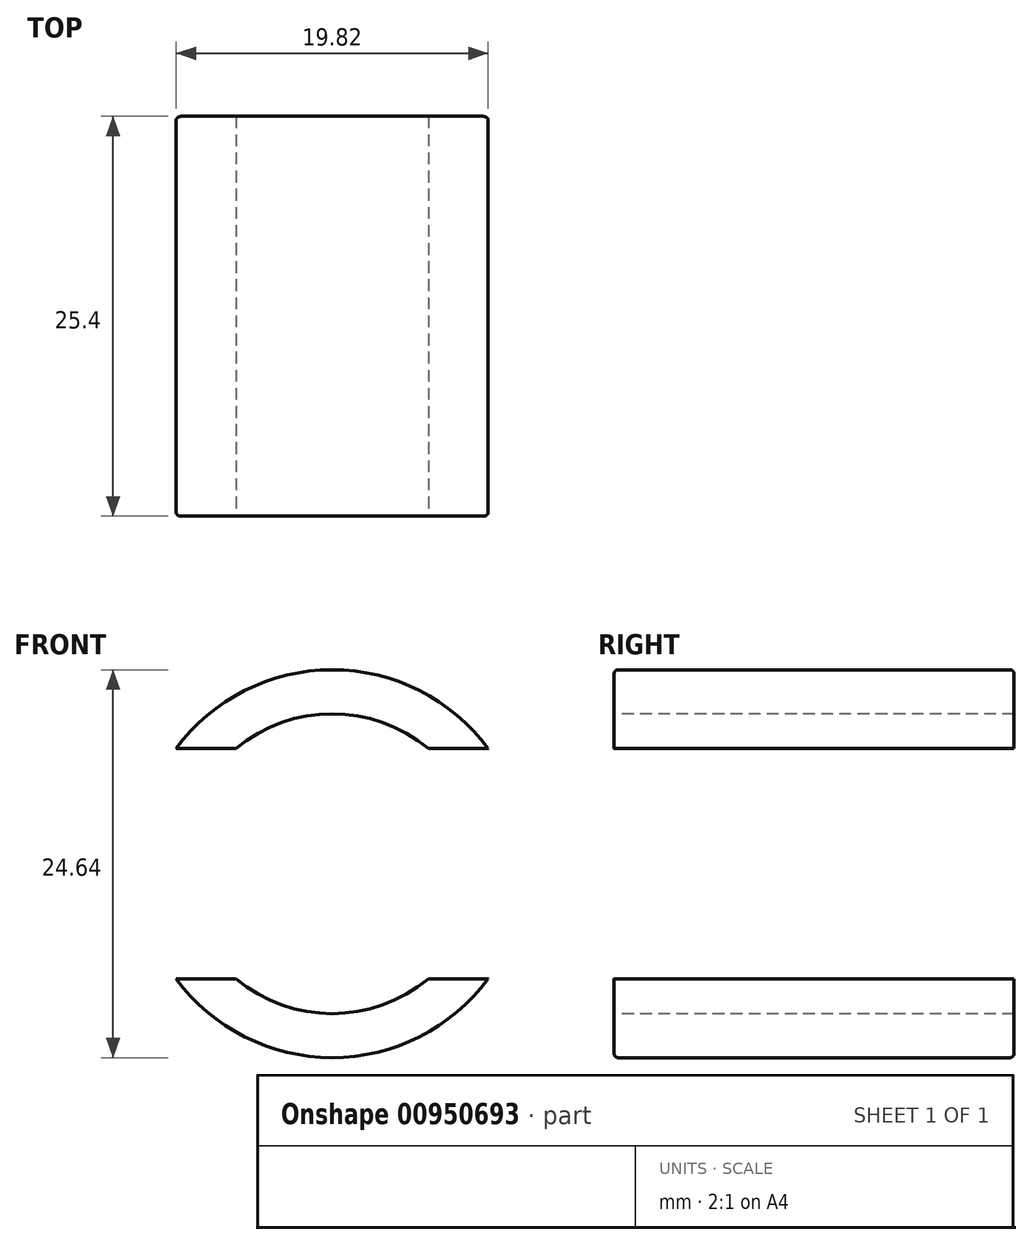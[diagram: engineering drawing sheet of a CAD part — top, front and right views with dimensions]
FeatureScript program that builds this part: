
annotation { "Feature Type Name" : "Feature", "Feature Type Description" : "" }
export const myFeature = defineFeature(function(context is Context, id is Id, definition is map)
    precondition{}
    {
        {
            var Q0;
            Q0=qCreatedBy(makeId("Front.planeOp"),FACE);
            var sketch = newSketch(context, id + "F0", { "sketchPlane" : qUnion([Q0])});
            skCircle(sketch, "E0", {"center": v(0, 0) * mm, "radius": 12.32 * mm});
            skSolve(sketch);
        }
        {
            var Q0;
            Q0 = qSketchRegion(id + "F0", true);
            extrude(context, id + "F1", {"entities" : qUnion([Q0]), "depth" : 25.4 * mm, "offsetDistance" : 25.4 * mm});
        }
        {
            var Q0;
            Q0=makeQuery(id+"F1.opExtrude","CAP_FACE",FACE,{"disambiguationData":[OSD([sQuery(id+"F0.wireOp",EDGE,"E0")])],"isStart":false});
            var sketch = newSketch(context, id + "F2", { "sketchPlane" : qUnion([Q0])});
            skPoint(sketch, "E1.middle", {"position": v(0, 0) * mm});
            skArc(sketch, "E2", {"start": v(9.91, 7.31) * mm, "mid": v(0, 12.32) * mm, "end": v(-9.91, 7.31) * mm});
            skArc(sketch, "E3", {"start": v(6.1, 7.31) * mm, "mid": v(0, 9.52) * mm, "end": v(-6.1, 7.31) * mm});
            skLineSegment(sketch, "E4", {"start": v(-6.1, 7.31) * mm, "end": v(-9.91, 7.31) * mm});
            skLineSegment(sketch, "E5", {"start": v(6.1, 7.31) * mm, "end": v(9.91, 7.31) * mm});
            skSolve(sketch);
        }
        {
            var Q0;
            Q0 = qSketchRegion(id + "F2", true);
            extrude(context, id + "F3", {"entities" : qUnion([Q0]), "operationType" : NewBodyOperationType.INTERSECT, "oppositeDirection" : true, "depth" : 25.4 * mm, "offsetDistance" : 25.4 * mm});
        }
        {
            var Q0;
            Q0=makeQuery(id+"F1.opExtrude","SWEPT_BODY",BODY,{"disambiguationData":[OSD([sQuery(id+"F0.wireOp",EDGE,"E0")])]});
            var Q1;
            Q1=qCreatedBy(makeId("Top.planeOp"),FACE);
            mirror(context, id + "F4", {"entities" : qUnion([Q0]), "mirrorPlane" : qUnion([Q1])});
        }
        {
            var Q0;
            Q0=makeQuery(id+"F1.opExtrude","CAP_EDGE",EDGE,{"disambiguationData":[OSD([sQuery(id+"F0.wireOp",EDGE,"E0")])],"isStart":false});
            var Q1;
            Q1=makeQuery(id+"F1.opExtrude","CAP_EDGE",EDGE,{"disambiguationData":[OSD([sQuery(id+"F0.wireOp",EDGE,"E0")])],"isStart":true});
            var Q2;
            Q2=makeQuery(id+"F4.opPattern","COPY",EDGE,{"derivedFrom":makeQuery(id+"F1.opExtrude","CAP_EDGE",EDGE,{"disambiguationData":[OSD([sQuery(id+"F0.wireOp",EDGE,"E0")])],"isStart":false}),"instanceName":"1"});
            var Q3;
            Q3=makeQuery(id+"F4.opPattern","COPY",EDGE,{"derivedFrom":makeQuery(id+"F1.opExtrude","CAP_EDGE",EDGE,{"disambiguationData":[OSD([sQuery(id+"F0.wireOp",EDGE,"E0")])],"isStart":true}),"instanceName":"1"});
            fillet(context, id + "F5", {"entities" : qUnion([Q0, Q1, Q2, Q3]), "radius" : 0.25 * mm, "tangentPropagation" : true, "allowEdgeOverflow" : false});
        }
    });
